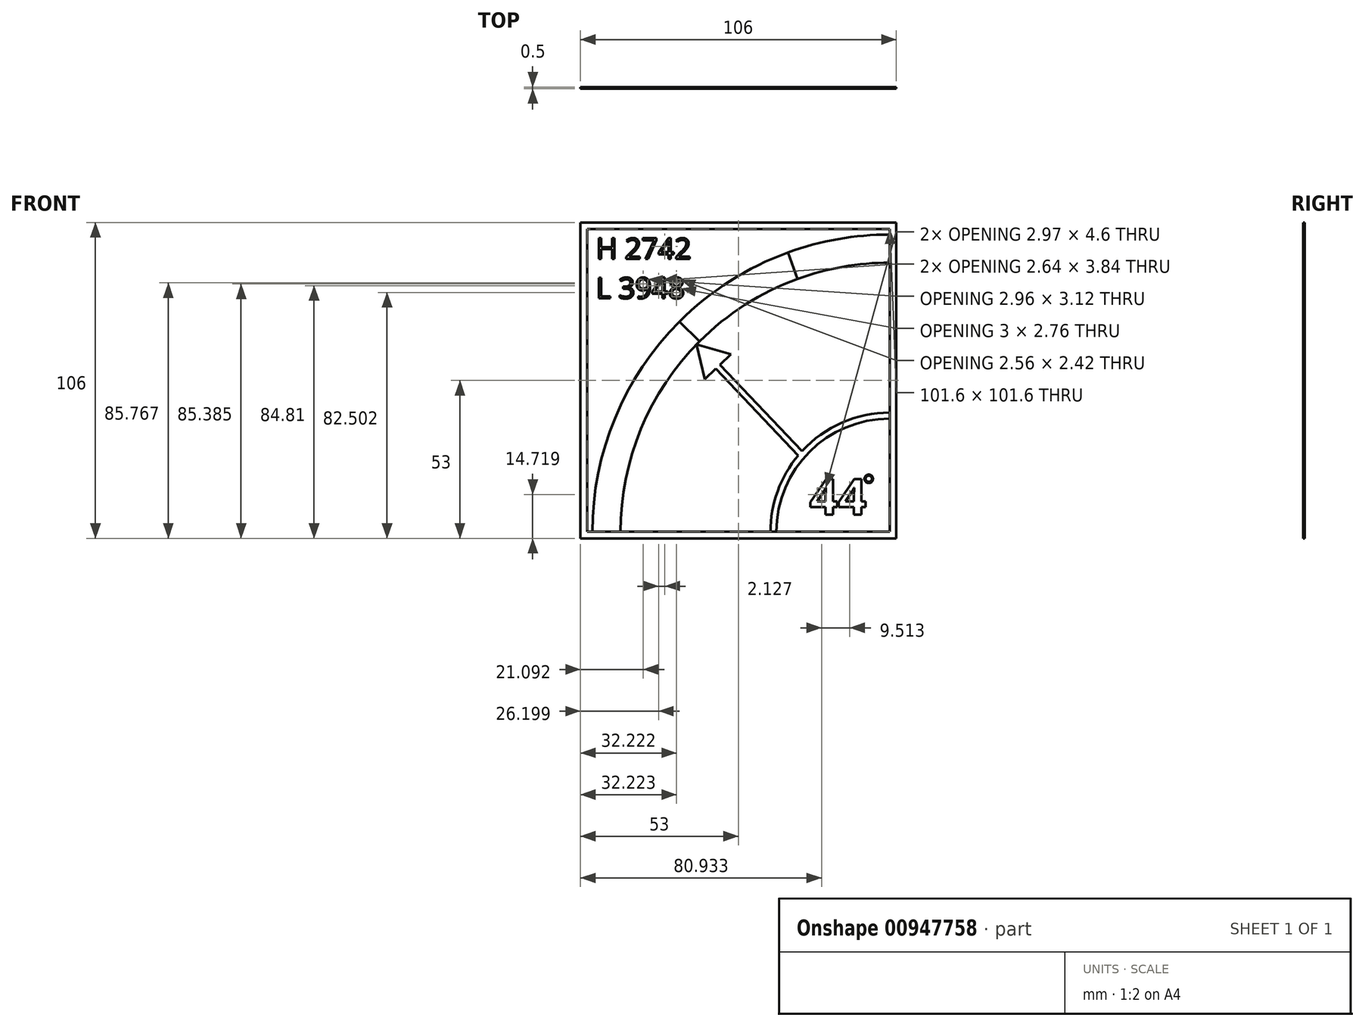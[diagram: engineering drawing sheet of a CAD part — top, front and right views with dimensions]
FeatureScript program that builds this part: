
annotation { "Feature Type Name" : "Feature", "Feature Type Description" : "" }
export const myFeature = defineFeature(function(context is Context, id is Id, definition is map)
    precondition{}
    {
        {
            var Q0;
            Q0=qCreatedBy(makeId("Front.planeOp"),FACE);
            var sketch = newSketch(context, id + "F0", { "sketchPlane" : qUnion([Q0])});
            skLineSegment(sketch, "E0.right", {"start": v(-50.8, -50.8) * mm, "end": v(-50.8, 50.8) * mm});
            skPoint(sketch, "E0.middle", {"position": v(0, 0) * mm});
            skArc(sketch, "E1", {"start": v(-49, -50.8) * mm, "mid": v(-19.77, 19.77) * mm, "end": v(50.8, 49) * mm});
            skLineSegment(sketch, "E2", {"start": v(50.8, -50.8) * mm, "end": v(16.67, 42.98) * mm, "construction": true});
            skArc(sketch, "E3", {"start": v(-39.55, -50.8) * mm, "mid": v(-32.67, -16.22) * mm, "end": v(-13.09, 13.09) * mm});
            skLineSegment(sketch, "E4", {"start": v(-49, -50.8) * mm, "end": v(-39.55, -50.8) * mm});
            skLineSegment(sketch, "E5", {"start": v(-50.8, 50.8) * mm, "end": v(50.8, 50.8) * mm, "construction": true});
            skLineSegment(sketch, "E6", {"start": v(50.8, 50.8) * mm, "end": v(50.8, -50.8) * mm, "construction": true});
            skLineSegment(sketch, "E7", {"start": v(50.8, -50.8) * mm, "end": v(-39.55, -50.8) * mm, "construction": true});
            skLineSegment(sketch, "E8", {"start": v(-19.77, 19.77) * mm, "end": v(-13.09, 13.09) * mm});
            skSolve(sketch);
        }
        {
            var Q0;
            Q0 = qSketchRegion(id + "F0", true);
            extrude(context, id + "F1", {"entities" : qUnion([Q0]), "depth" : .5 * mm, "offsetDistance" : 25 * mm});
        }
        {
            var Q0;
            Q0=qCreatedBy(makeId("Front.planeOp"),FACE);
            var sketch = newSketch(context, id + "F2", { "sketchPlane" : qUnion([Q0])});
            skPoint(sketch, "E9", {"position": v(50.8, -50.8) * mm});
            skArc(sketch, "E10", {"start": v(-19.77, 19.77) * mm, "mid": v(-2.82, 33.37) * mm, "end": v(16.67, 42.98) * mm});
            skArc(sketch, "E11", {"start": v(-13.09, 13.09) * mm, "mid": v(2.25, 25.4) * mm, "end": v(19.9, 34.1) * mm});
            skLineSegment(sketch, "E12", {"start": v(16.67, 42.98) * mm, "end": v(19.9, 34.1) * mm});
            skLineSegment(sketch, "E13", {"start": v(-19.77, 19.77) * mm, "end": v(-13.09, 13.09) * mm});
            skSolve(sketch);
        }
        {
            var Q0;
            Q0 = qSketchRegion(id + "F2", true);
            extrude(context, id + "F3", {"entities" : qUnion([Q0]), "depth" : .5 * mm, "offsetDistance" : 25 * mm});
        }
        {
            var Q0;
            Q0=qCreatedBy(makeId("Front.planeOp"),FACE);
            var sketch = newSketch(context, id + "F4", { "sketchPlane" : qUnion([Q0])});
            skPoint(sketch, "E14", {"position": v(50.8, -50.8) * mm});
            skArc(sketch, "E15", {"start": v(16.67, 42.98) * mm, "mid": v(33.47, 47.48) * mm, "end": v(50.8, 49) * mm});
            skArc(sketch, "E16", {"start": v(19.9, 34.1) * mm, "mid": v(35.11, 38.18) * mm, "end": v(50.8, 39.55) * mm});
            skLineSegment(sketch, "E17", {"start": v(50.8, 49) * mm, "end": v(50.8, 39.55) * mm});
            skLineSegment(sketch, "E18", {"start": v(16.67, 42.98) * mm, "end": v(19.9, 34.1) * mm});
            skSolve(sketch);
        }
        {
            var Q0;
            Q0 = qSketchRegion(id + "F4", true);
            extrude(context, id + "F5", {"entities" : qUnion([Q0]), "depth" : .2 * mm, "offsetDistance" : 25 * mm});
        }
        {
            var Q0;
            Q0=qCreatedBy(makeId("Front.planeOp"),FACE);
            var sketch = newSketch(context, id + "F6", { "sketchPlane" : qUnion([Q0])});
            skLineSegment(sketch, "E19.bottom", {"start": v(-50.8, 50.8) * mm, "end": v(50.8, 50.8) * mm});
            skLineSegment(sketch, "E19.top", {"start": v(-50.8, -50.8) * mm, "end": v(50.8, -50.8) * mm});
            skLineSegment(sketch, "E19.left", {"start": v(-50.8, 50.8) * mm, "end": v(-50.8, -50.8) * mm});
            skLineSegment(sketch, "E19.right", {"start": v(50.8, 50.8) * mm, "end": v(50.8, -50.8) * mm});
            skLineSegment(sketch, "E20.bottom", {"start": v(53, -53) * mm, "end": v(-53, -53) * mm});
            skLineSegment(sketch, "E20.top", {"start": v(53, 53) * mm, "end": v(-53, 53) * mm});
            skLineSegment(sketch, "E20.left", {"start": v(53, -53) * mm, "end": v(53, 53) * mm});
            skLineSegment(sketch, "E20.right", {"start": v(-53, -53) * mm, "end": v(-53, 53) * mm});
            skSolve(sketch);
        }
        {
            var Q0;
            Q0 = qSketchRegion(id + "F6", true);
            extrude(context, id + "F7", {"entities" : qUnion([Q0]), "depth" : .5 * mm, "offsetDistance" : 25 * mm});
        }
        {
            var Q0;
            Q0=qCreatedBy(makeId("Front.planeOp"),FACE);
            var sketch = newSketch(context, id + "F8", { "sketchPlane" : qUnion([Q0])});
            skPoint(sketch, "E21.middle", {"position": v(-65.48, 20.07) * mm});
            skLineSegment(sketch, "E22", {"start": v(-6.13, 5.3) * mm, "end": v(-2.5, 8.75) * mm});
            skLineSegment(sketch, "E23", {"start": v(-7.58, 3.93) * mm, "end": v(-11.2, 0.48) * mm});
            skLineSegment(sketch, "E24", {"start": v(-11.2, 0.48) * mm, "end": v(-14.02, 12.15) * mm});
            skLineSegment(sketch, "E25", {"start": v(-14.02, 12.15) * mm, "end": v(-2.5, 8.75) * mm});
            skLineSegment(sketch, "E26", {"start": v(-6.85, 4.62) * mm, "end": v(20.75, -24.4) * mm, "construction": true});
            skLineSegment(sketch, "E27", {"start": v(-7.58, 3.93) * mm, "end": v(20.1, -25.16) * mm});
            skLineSegment(sketch, "E28", {"start": v(-6.13, 5.3) * mm, "end": v(21.42, -23.65) * mm});
            skArc(sketch, "E29", {"start": v(10.8, -50.8) * mm, "mid": v(22.52, -22.52) * mm, "end": v(50.8, -10.8) * mm});
            skArc(sketch, "E30", {"start": v(12.8, -50.8) * mm, "mid": v(23.93, -23.93) * mm, "end": v(50.8, -12.8) * mm});
            skLineSegment(sketch, "E31", {"start": v(50.8, -10.8) * mm, "end": v(50.8, -12.8) * mm});
            skLineSegment(sketch, "E32", {"start": v(10.8, -50.8) * mm, "end": v(12.8, -50.8) * mm});
            skText(sketch, "E33", { "text": "44", "fontName": "OpenSans-Bold.ttf"});
            skText(sketch, "E34", { "text": "H 2742\nL 3948", "fontName": "OpenSans-Regular.ttf"});
            skCircle(sketch, "E35", {"center": v(43.8, -33) * mm, "radius": 1.43 * mm});
            skCircle(sketch, "E36", {"center": v(43.8, -33) * mm, "radius": 1.04 * mm});
            const initialGuessF8  = {"E33": [0.02395, -0.045, 1, 0, 0.012], "E34": [-0.0478, 0.0408, 1, 0, 0.007]};
            skSetInitialGuess(sketch, initialGuessF8);
            skSolve(sketch);
        }
        {
            var Q0;
            Q0 = qSketchRegion(id + "F8", true);
            extrude(context, id + "F9", {"entities" : qUnion([Q0]), "depth" : .5 * mm, "offsetDistance" : 25 * mm});
        }
    });
